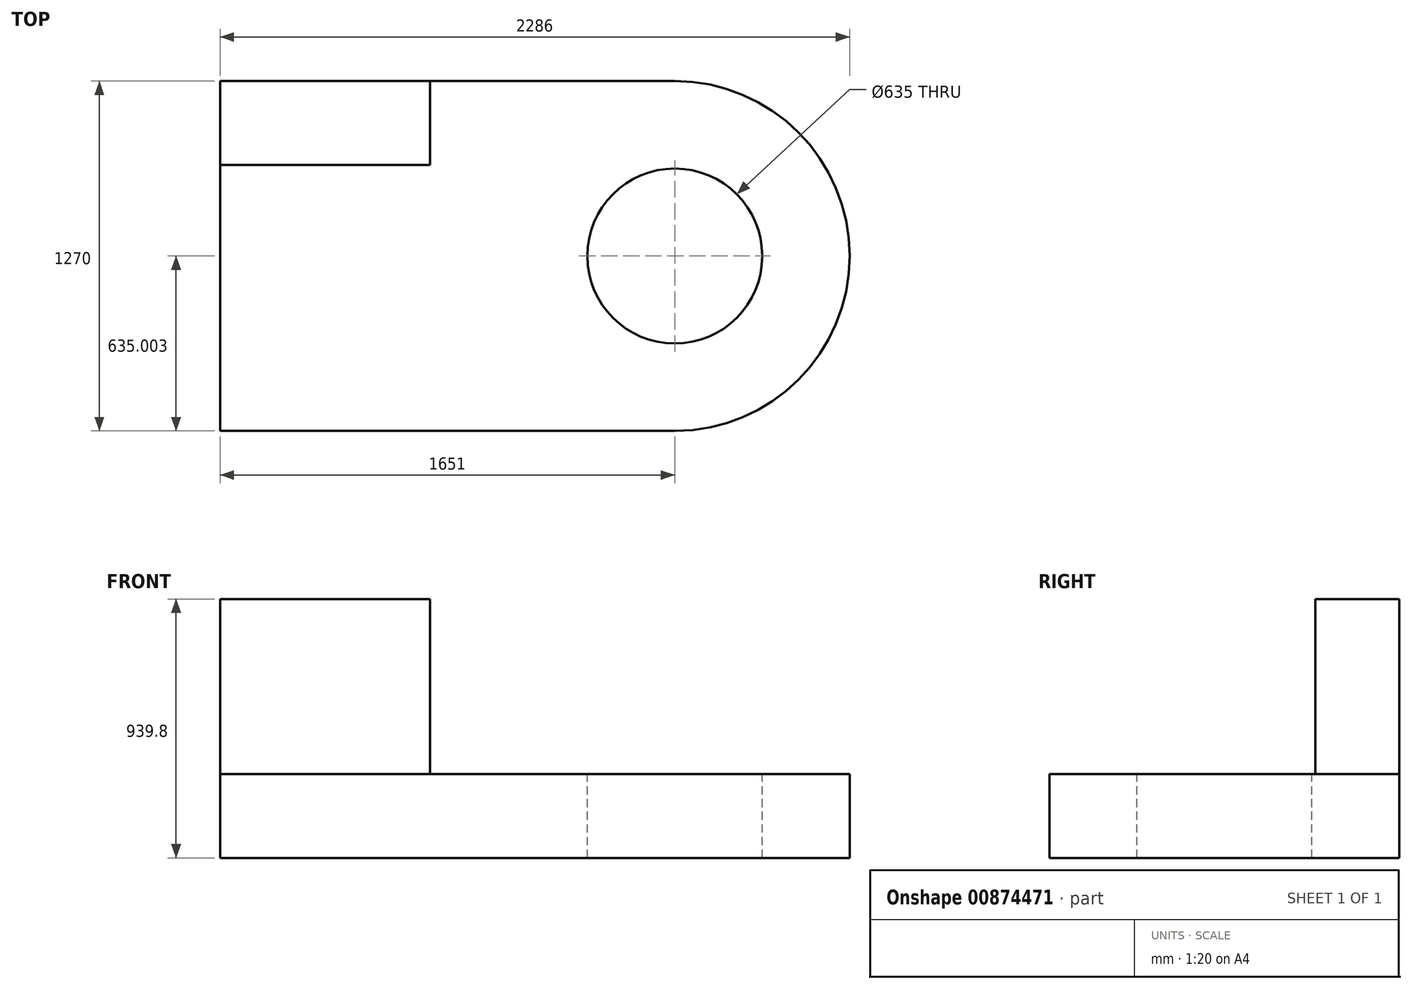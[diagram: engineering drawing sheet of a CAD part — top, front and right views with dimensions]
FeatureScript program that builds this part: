
annotation { "Feature Type Name" : "Feature", "Feature Type Description" : "" }
export const myFeature = defineFeature(function(context is Context, id is Id, definition is map)
    precondition{}
    {
        {
            var Q0;
            Q0=qCreatedBy(makeId("Top.planeOp"),FACE);
            var sketch = newSketch(context, id + "F0", { "sketchPlane" : qUnion([Q0])});
            skLineSegment(sketch, "E0.bottom", {"start": v(-54.8, -47.48) * mm, "end": v(1596.2, -47.48) * mm});
            skLineSegment(sketch, "E0.top", {"start": v(-54.8, 1222.52) * mm, "end": v(1596.2, 1222.52) * mm});
            skLineSegment(sketch, "E0.left", {"start": v(-54.8, -47.48) * mm, "end": v(-54.8, 1222.52) * mm});
            skLineSegment(sketch, "E0.right", {"start": v(1596.2, -47.48) * mm, "end": v(1596.2, 1222.52) * mm});
            skSolve(sketch);
        }
        {
            var Q0;
            Q0=makeQuery(id+"F0.imprint","IMPRINT",FACE,{"disambiguationData":[TD([[makeQuery(id+"F0.imprint","IMPRINT",EDGE,{"derivedFrom":sQuery(id+"F0.wireOp",EDGE,"E0.bottom")}),1.0]])]});
            extrude(context, id + "F1", {"entities" : qUnion([Q0]), "depth" : 304.8 * mm, "offsetDistance" : 25.4 * mm});
        }
        {
            var Q0;
            Q0=makeQuery(id+"F1.opExtrude","CAP_FACE",FACE,{"disambiguationData":[OSD([sQuery(id+"F0.wireOp",EDGE,"E0.bottom"),sQuery(id+"F0.wireOp",EDGE,"E0.top"),sQuery(id+"F0.wireOp",EDGE,"E0.left"),sQuery(id+"F0.wireOp",EDGE,"E0.right")])],"isStart":false});
            var sketch = newSketch(context, id + "F2", { "sketchPlane" : qUnion([Q0])});
            skLineSegment(sketch, "E1.bottom", {"start": v(-54.8, 1222.52) * mm, "end": v(707.2, 1222.52) * mm});
            skLineSegment(sketch, "E1.top", {"start": v(-54.8, 917.72) * mm, "end": v(707.2, 917.72) * mm});
            skLineSegment(sketch, "E1.left", {"start": v(-54.8, 1222.52) * mm, "end": v(-54.8, 917.72) * mm});
            skLineSegment(sketch, "E1.right", {"start": v(707.2, 1222.52) * mm, "end": v(707.2, 917.72) * mm});
            skSolve(sketch);
        }
        {
            var Q0;
            Q0=makeQuery(id+"F2.imprint","IMPRINT",FACE,{"disambiguationData":[TD([[makeQuery(id+"F2.imprint","IMPRINT",EDGE,{"derivedFrom":sQuery(id+"F2.wireOp",EDGE,"E1.bottom")}),-1.0]])]});
            extrude(context, id + "F3", {"entities" : qUnion([Q0]), "operationType" : NewBodyOperationType.ADD, "depth" : 635 * mm, "offsetDistance" : 25.4 * mm});
        }
        {
            var Q0;
            Q0=makeQuery(id+"F1.opExtrude","CAP_FACE",FACE,{"disambiguationData":[OSD([sQuery(id+"F0.wireOp",EDGE,"E0.bottom"),sQuery(id+"F0.wireOp",EDGE,"E0.top"),sQuery(id+"F0.wireOp",EDGE,"E0.left"),sQuery(id+"F0.wireOp",EDGE,"E0.right")])],"isStart":false});
            var sketch = newSketch(context, id + "F4", { "sketchPlane" : qUnion([Q0])});
            skCircle(sketch, "E2", {"center": v(1596.2, 587.52) * mm, "radius": 635 * mm});
            skSolve(sketch);
        }
        {
            var Q0;
            Q0 = qSketchRegion(id + "F4", true);
            extrude(context, id + "F5", {"entities" : qUnion([Q0]), "operationType" : NewBodyOperationType.ADD, "oppositeDirection" : true, "depth" : 304.8 * mm, "offsetDistance" : 25.4 * mm});
        }
        {
            var Q0;
            Q0=makeQuery(id+"F5.boolean.opBoolean","MERGE",FACE,{"derivedFrom":[makeQuery(id+"F1.opExtrude","CAP_FACE",FACE,{"disambiguationData":[OSD([sQuery(id+"F0.wireOp",EDGE,"E0.bottom"),sQuery(id+"F0.wireOp",EDGE,"E0.top"),sQuery(id+"F0.wireOp",EDGE,"E0.left"),sQuery(id+"F0.wireOp",EDGE,"E0.right")])],"isStart":false}),makeQuery(id+"F5.opExtrude","CAP_FACE",FACE,{"disambiguationData":[OSD([sQuery(id+"F4.wireOp",EDGE,"E2")])],"isStart":true})]});
            var sketch = newSketch(context, id + "F6", { "sketchPlane" : qUnion([Q0])});
            skCircle(sketch, "E3", {"center": v(1596.2, 587.52) * mm, "radius": 317.5 * mm});
            skSolve(sketch);
        }
        {
            var Q0;
            Q0 = qSketchRegion(id + "F6", true);
            extrude(context, id + "F7", {"entities" : qUnion([Q0]), "operationType" : NewBodyOperationType.REMOVE, "oppositeDirection" : true, "depth" : 355.6 * mm, "offsetDistance" : 25.4 * mm});
        }
    });
